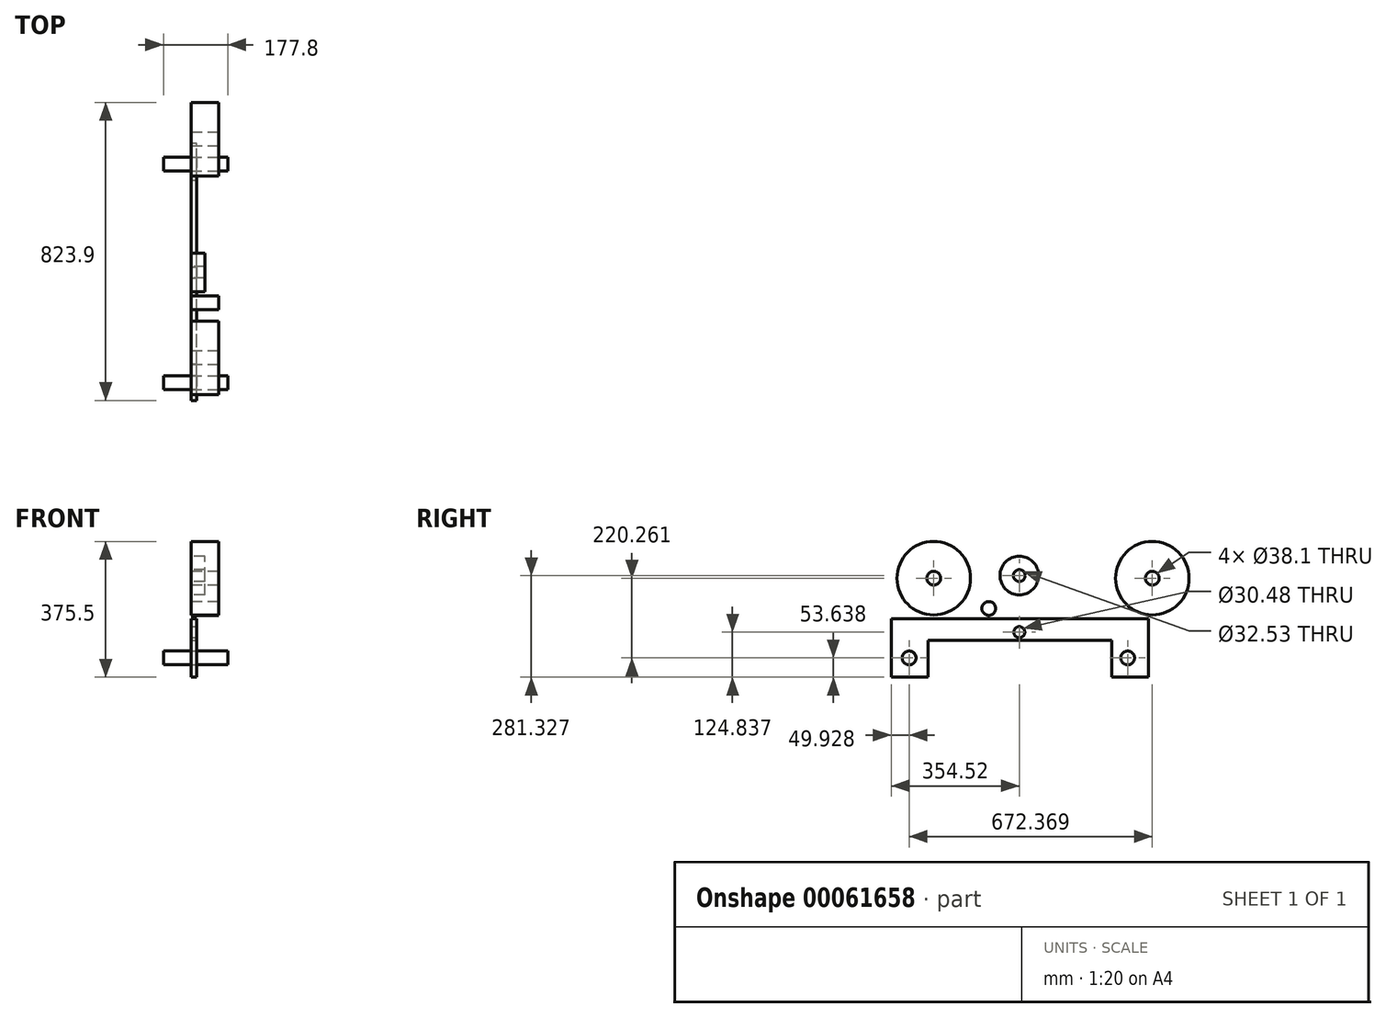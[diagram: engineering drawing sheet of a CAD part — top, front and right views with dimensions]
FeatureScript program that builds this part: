
annotation { "Feature Type Name" : "Feature", "Feature Type Description" : "" }
export const myFeature = defineFeature(function(context is Context, id is Id, definition is map)
    precondition{}
    {
        {
            var Q0;
            Q0=qCreatedBy(makeId("Right.planeOp"),FACE);
            var sketch = newSketch(context, id + "F0", { "sketchPlane" : qUnion([Q0])});
            skLineSegment(sketch, "E0.bottom", {"start": v(-354.52, 0) * mm, "end": v(356.68, 0) * mm});
            skLineSegment(sketch, "E0.top", {"start": v(-354.52, 60.88) * mm, "end": v(356.68, 60.88) * mm});
            skLineSegment(sketch, "E0.left", {"start": v(-354.52, 0) * mm, "end": v(-354.52, 60.88) * mm});
            skLineSegment(sketch, "E0.right", {"start": v(356.68, 0) * mm, "end": v(356.68, 60.88) * mm});
            skSolve(sketch);
        }
        {
            var Q0;
            Q0 = qSketchRegion(id + "F0", true);
            extrude(context, id + "F1", {"entities" : qUnion([Q0]), "depth" : 15.88 * mm});
        }
        {
            var Q0;
            Q0=makeQuery(id+"F1.opExtrude","SWEPT_FACE",FACE,{"disambiguationData":[OSD([sQuery(id+"F0.wireOp",EDGE,"E0.bottom")])]});
            var sketch = newSketch(context, id + "F2", { "sketchPlane" : qUnion([Q0])});
            skLineSegment(sketch, "E1.bottom", {"start": v(0, 354.52) * mm, "end": v(15.87, 354.52) * mm});
            skLineSegment(sketch, "E1.top", {"start": v(0, 252.92) * mm, "end": v(15.88, 252.92) * mm});
            skLineSegment(sketch, "E1.left", {"start": v(0, 354.52) * mm, "end": v(0, 252.92) * mm});
            skLineSegment(sketch, "E1.right", {"start": v(15.88, 354.52) * mm, "end": v(15.88, 252.92) * mm});
            skLineSegment(sketch, "E2.bottom", {"start": v(0, -356.68) * mm, "end": v(15.88, -356.68) * mm});
            skLineSegment(sketch, "E2.top", {"start": v(0, -255.08) * mm, "end": v(15.88, -255.08) * mm});
            skLineSegment(sketch, "E2.left", {"start": v(0, -356.68) * mm, "end": v(0, -255.08) * mm});
            skLineSegment(sketch, "E2.right", {"start": v(15.88, -356.68) * mm, "end": v(15.88, -255.08) * mm});
            skSolve(sketch);
        }
        {
            var Q0;
            Q0 = qSketchRegion(id + "F2", true);
            extrude(context, id + "F3", {"entities" : qUnion([Q0]), "operationType" : NewBodyOperationType.ADD, "depth" : 101.6 * mm});
        }
        {
            var Q0;
            Q0=makeQuery(id+"F3.boolean.opBoolean","MERGE",FACE,{"derivedFrom":[makeQuery(id+"F1.opExtrude","CAP_FACE",FACE,{"disambiguationData":[OSD([sQuery(id+"F0.wireOp",EDGE,"E0.bottom"),sQuery(id+"F0.wireOp",EDGE,"E0.top"),sQuery(id+"F0.wireOp",EDGE,"E0.left"),sQuery(id+"F0.wireOp",EDGE,"E0.right")])],"isStart":false}),makeQuery(id+"F3.opExtrude","SWEPT_FACE",FACE,{"disambiguationData":[OSD([sQuery(id+"F2.wireOp",EDGE,"E1.right")])]}),makeQuery(id+"F3.opExtrude","SWEPT_FACE",FACE,{"disambiguationData":[OSD([sQuery(id+"F2.wireOp",EDGE,"E2.right")])]})]});
            var sketch = newSketch(context, id + "F4", { "sketchPlane" : qUnion([Q0])});
            skCircle(sketch, "E3", {"center": v(0, 23.24) * mm, "radius": 15.24 * mm});
            skSolve(sketch);
        }
        {
            var Q0;
            Q0 = qSketchRegion(id + "F4", true);
            extrude(context, id + "F5", {"entities" : qUnion([Q0]), "operationType" : NewBodyOperationType.REMOVE, "endBound" : BoundingType.THROUGH_ALL, "oppositeDirection" : true, "depth" : 25.4 * mm});
        }
        {
            var Q0;
            Q0=makeQuery(id+"F3.boolean.opBoolean","MERGE",FACE,{"derivedFrom":[makeQuery(id+"F1.opExtrude","CAP_FACE",FACE,{"disambiguationData":[OSD([sQuery(id+"F0.wireOp",EDGE,"E0.bottom"),sQuery(id+"F0.wireOp",EDGE,"E0.top"),sQuery(id+"F0.wireOp",EDGE,"E0.left"),sQuery(id+"F0.wireOp",EDGE,"E0.right")])],"isStart":false}),makeQuery(id+"F3.opExtrude","SWEPT_FACE",FACE,{"disambiguationData":[OSD([sQuery(id+"F2.wireOp",EDGE,"E1.right")])]}),makeQuery(id+"F3.opExtrude","SWEPT_FACE",FACE,{"disambiguationData":[OSD([sQuery(id+"F2.wireOp",EDGE,"E2.right")])]})]});
            var sketch = newSketch(context, id + "F6", { "sketchPlane" : qUnion([Q0])});
            skCircle(sketch, "E4", {"center": v(-304.6, -47.96) * mm, "radius": 19.05 * mm});
            skCircle(sketch, "E5.1.0.0", {"center": v(299.78, -47.96) * mm, "radius": 19.05 * mm});
            skLineSegment(sketch, "E5.direction1", {"start": v(-304.6, -47.96) * mm, "end": v(299.78, -47.96) * mm, "construction": true});
            skSolve(sketch);
        }
        {
            var Q0;
            Q0 = qSketchRegion(id + "F6", true);
            extrude(context, id + "F7", {"entities" : qUnion([Q0]), "operationType" : NewBodyOperationType.REMOVE, "endBound" : BoundingType.THROUGH_ALL, "oppositeDirection" : true, "depth" : 25.4 * mm});
        }
        {
            var Q0;
            Q0=qCreatedBy(makeId("Right.planeOp"),FACE);
            var sketch = newSketch(context, id + "F8", { "sketchPlane" : qUnion([Q0])});
            skCircle(sketch, "E6", {"center": v(299.78, -47.96) * mm, "radius": 19.05 * mm});
            skCircle(sketch, "E7.1.0.0", {"center": v(-304.81, -47.96) * mm, "radius": 19.05 * mm});
            skLineSegment(sketch, "E7.direction1", {"start": v(299.78, -47.96) * mm, "end": v(-304.81, -47.96) * mm, "construction": true});
            skSolve(sketch);
        }
        {
            var Q0;
            Q0 = qSketchRegion(id + "F8", true);
            extrude(context, id + "F9", {"entities" : qUnion([Q0]), "oppositeDirection" : true, "depth" : 76.2 * mm, "hasSecondDirection" : true, "secondDirectionOppositeDirection" : false, "secondDirectionDepth" : 101.6 * mm});
        }
        {
            var Q0;
            Q0=qCreatedBy(makeId("Right.planeOp"),FACE);
            var sketch = newSketch(context, id + "F10", { "sketchPlane" : qUnion([Q0])});
            skCircle(sketch, "E8", {"center": v(-236.82, 172.3) * mm, "radius": 101.6 * mm});
            skCircle(sketch, "E9.1.0.0", {"center": v(367.78, 172.3) * mm, "radius": 101.6 * mm});
            skLineSegment(sketch, "E9.direction1", {"start": v(-236.82, 172.3) * mm, "end": v(367.78, 172.3) * mm, "construction": true});
            skCircle(sketch, "E10", {"center": v(-236.82, 172.3) * mm, "radius": 19.05 * mm});
            skCircle(sketch, "E11.1.0.0", {"center": v(367.78, 172.3) * mm, "radius": 19.05 * mm});
            skSolve(sketch);
        }
        {
            var Q0;
            Q0 = qSketchRegion(id + "F10", true);
            extrude(context, id + "F11", {"entities" : qUnion([Q0]), "depth" : 76.2 * mm});
        }
        {
            var Q0;
            Q0=qCreatedBy(makeId("Right.planeOp"),FACE);
            var sketch = newSketch(context, id + "F12", { "sketchPlane" : qUnion([Q0])});
            skCircle(sketch, "E12", {"center": v(0, 179.73) * mm, "radius": 53.43 * mm});
            skCircle(sketch, "E13", {"center": v(0, 179.73) * mm, "radius": 16.26 * mm});
            skSolve(sketch);
        }
        {
            var Q0;
            Q0 = qSketchRegion(id + "F12", true);
            extrude(context, id + "F13", {"entities" : qUnion([Q0]), "depth" : 38.1 * mm});
        }
        {
            var Q0;
            Q0=qCreatedBy(makeId("Right.planeOp"),FACE);
            var sketch = newSketch(context, id + "F14", { "sketchPlane" : qUnion([Q0])});
            skCircle(sketch, "E14", {"center": v(-84.5, 88.7) * mm, "radius": 19.05 * mm});
            skSolve(sketch);
        }
        {
            var Q0;
            Q0 = qSketchRegion(id + "F14", true);
            extrude(context, id + "F15", {"entities" : qUnion([Q0]), "depth" : 76.2 * mm});
        }
    });
